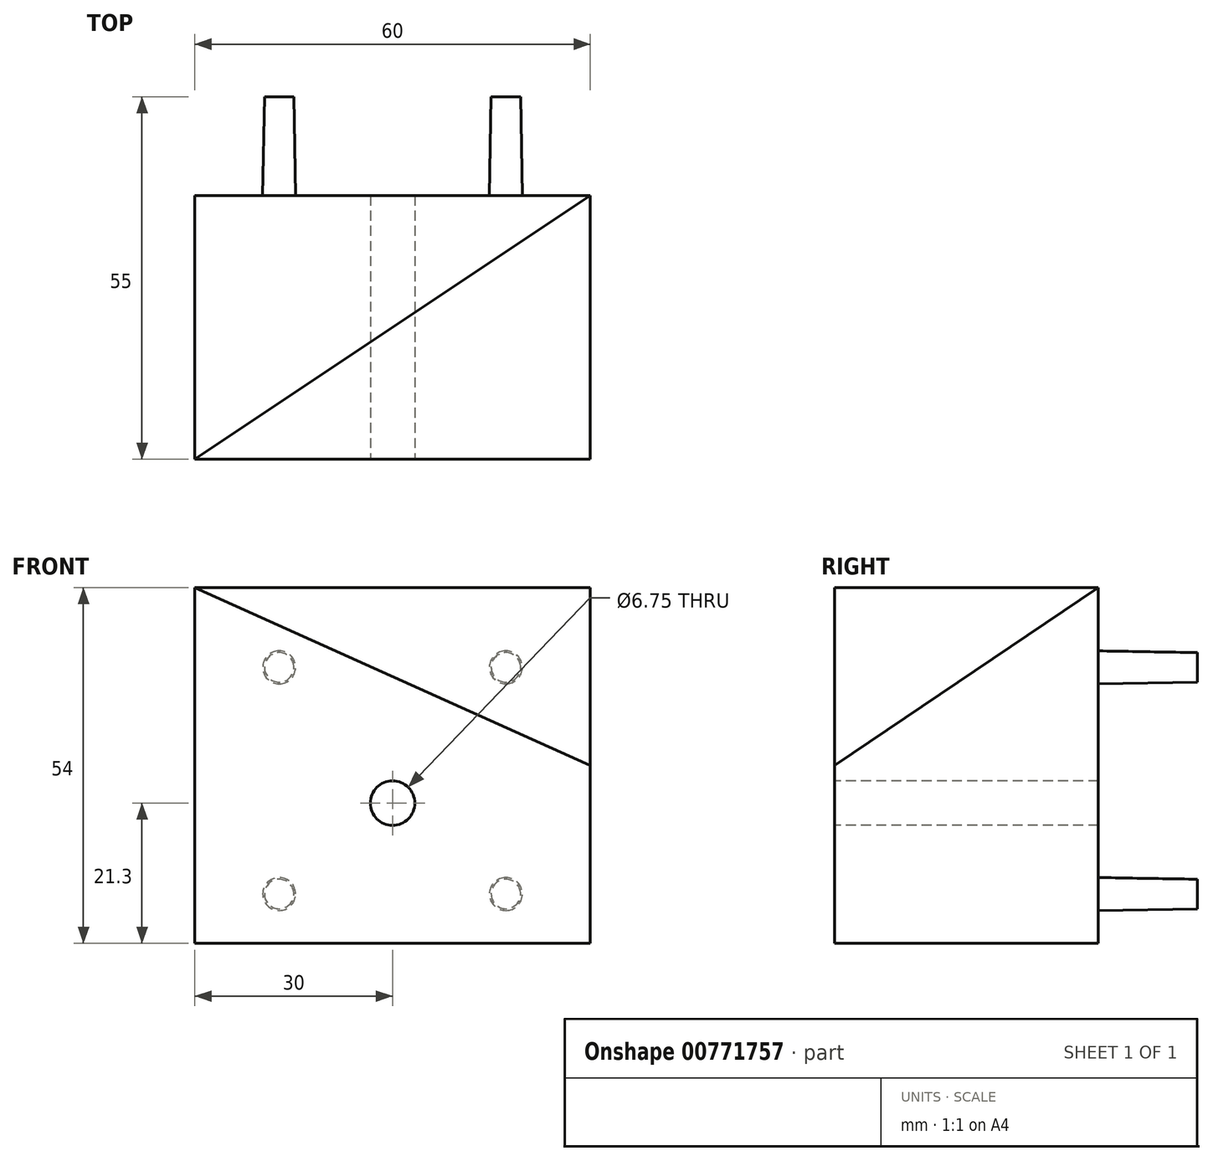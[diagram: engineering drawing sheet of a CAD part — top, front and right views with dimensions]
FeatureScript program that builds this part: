
annotation { "Feature Type Name" : "Feature", "Feature Type Description" : "" }
export const myFeature = defineFeature(function(context is Context, id is Id, definition is map)
    precondition{}
    {
        {
            var Q0;
            Q0=qCreatedBy(makeId("Front.planeOp"),FACE);
            var sketch = newSketch(context, id + "F0", { "sketchPlane" : qUnion([Q0])});
            skLineSegment(sketch, "E0.bottom", {"start": v(30, 27) * mm, "end": v(-30, 27) * mm});
            skLineSegment(sketch, "E0.top", {"start": v(30, -27) * mm, "end": v(-30, -27) * mm});
            skLineSegment(sketch, "E0.left", {"start": v(30, 27) * mm, "end": v(30, -27) * mm});
            skLineSegment(sketch, "E0.right", {"start": v(-30, 27) * mm, "end": v(-30, -27) * mm});
            skPoint(sketch, "E0.middle", {"position": v(0, 0) * mm});
            skSolve(sketch);
        }
        {
            var Q0;
            Q0=makeQuery(id+"F0.imprint","IMPRINT",FACE,{"disambiguationData":[TD([[makeQuery(id+"F0.imprint","IMPRINT",EDGE,{"derivedFrom":sQuery(id+"F0.wireOp",EDGE,"E0.bottom")}),1.0]])]});
            extrude(context, id + "F1", {"entities" : qUnion([Q0]), "depth" : 40 * mm, "offsetDistance" : 25 * mm});
        }
        {
            var Q0;
            Q0=makeQuery(id+"F1.opExtrude","CAP_FACE",FACE,{"disambiguationData":[OSD([sQuery(id+"F0.wireOp",EDGE,"E0.bottom"),sQuery(id+"F0.wireOp",EDGE,"E0.top"),sQuery(id+"F0.wireOp",EDGE,"E0.left"),sQuery(id+"F0.wireOp",EDGE,"E0.right")])],"isStart":true});
            var sketch = newSketch(context, id + "F2", { "sketchPlane" : qUnion([Q0])});
            skCircle(sketch, "E1", {"center": v(17.2, -19.5) * mm, "radius": 2.5 * mm});
            skCircle(sketch, "E2", {"center": v(-17.2, -19.5) * mm, "radius": 2.5 * mm});
            skCircle(sketch, "E3", {"center": v(-17.2, 14.9) * mm, "radius": 2.5 * mm});
            skCircle(sketch, "E4", {"center": v(17.2, 14.9) * mm, "radius": 2.5 * mm});
            skLineSegment(sketch, "E5", {"start": v(0, 0) * mm, "end": v(0, -31.74) * mm, "construction": true});
            skSolve(sketch);
        }
        {
            var Q0;
            Q0=makeQuery(id+"F2.imprint","IMPRINT",FACE,{"disambiguationData":[TD([[makeQuery(id+"F2.imprint","IMPRINT",EDGE,{"derivedFrom":sQuery(id+"F2.wireOp",EDGE,"E3")}),1.0]])]});
            var Q1;
            Q1=makeQuery(id+"F2.imprint","IMPRINT",FACE,{"disambiguationData":[TD([[makeQuery(id+"F2.imprint","IMPRINT",EDGE,{"derivedFrom":sQuery(id+"F2.wireOp",EDGE,"E4")}),1.0]])]});
            var Q2;
            Q2=makeQuery(id+"F2.imprint","IMPRINT",FACE,{"disambiguationData":[TD([[makeQuery(id+"F2.imprint","IMPRINT",EDGE,{"derivedFrom":sQuery(id+"F2.wireOp",EDGE,"E1")}),1.0]])]});
            var Q3;
            Q3=makeQuery(id+"F2.imprint","IMPRINT",FACE,{"disambiguationData":[TD([[makeQuery(id+"F2.imprint","IMPRINT",EDGE,{"derivedFrom":sQuery(id+"F2.wireOp",EDGE,"E2")}),1.0]])]});
            extrude(context, id + "F3", {"entities" : qUnion([Q0, Q1, Q2, Q3]), "operationType" : NewBodyOperationType.ADD, "depth" : 15 * mm, "offsetDistance" : 25 * mm, "hasDraft" : true, "draftAngle" : 1 * degree, "draftPullDirection" : true});
        }
        {
            var Q0;
            Q0=makeQuery(id+"F1.opExtrude","CAP_FACE",FACE,{"disambiguationData":[OSD([sQuery(id+"F0.wireOp",EDGE,"E0.bottom"),sQuery(id+"F0.wireOp",EDGE,"E0.top"),sQuery(id+"F0.wireOp",EDGE,"E0.left"),sQuery(id+"F0.wireOp",EDGE,"E0.right")])],"isStart":false});
            var sketch = newSketch(context, id + "F4", { "sketchPlane" : qUnion([Q0])});
            skCircle(sketch, "E6", {"center": v(0, -5.7) * mm, "radius": 3.38 * mm});
            skPoint(sketch, "E6.centerSnap0", {"position": v(0, -27) * mm});
            skSolve(sketch);
        }
        {
            var Q0;
            Q0=makeQuery(id+"F4.imprint","IMPRINT",FACE,{"disambiguationData":[TD([[makeQuery(id+"F4.imprint","IMPRINT",EDGE,{"derivedFrom":sQuery(id+"F4.wireOp",EDGE,"E6")}),1.0]])]});
            var Q1;
            Q1=makeQuery(id+"F1.opExtrude","CAP_FACE",FACE,{"disambiguationData":[OSD([sQuery(id+"F0.wireOp",EDGE,"E0.bottom"),sQuery(id+"F0.wireOp",EDGE,"E0.top"),sQuery(id+"F0.wireOp",EDGE,"E0.left"),sQuery(id+"F0.wireOp",EDGE,"E0.right")])],"isStart":true});
            extrude(context, id + "F5", {"entities" : qUnion([Q0]), "operationType" : NewBodyOperationType.REMOVE, "endBound" : BoundingType.UP_TO_SURFACE, "oppositeDirection" : true, "depth" : 25 * mm, "endBoundEntityFace" : qUnion([Q1]), "offsetDistance" : 25 * mm});
        }
        {
            var Q0;
            Q0=makeQuery(id+"F1.opExtrude","CAP_EDGE",EDGE,{"disambiguationData":[OSD([sQuery(id+"F0.wireOp",EDGE,"E0.left")])],"isStart":false});
            cPoint(context, id + "F6", {"entities" : qUnion([Q0]), "parameter" : 0.5});
        }
        {
            var Q0;
            Q0=makeQuery(id+"F1.opExtrude","CAP_VERTEX",VERTEX,{"disambiguationData":[OSD([sQuery(id+"F0.wireOp",EDGE,"E0.bottom"),sQuery(id+"F0.wireOp",EDGE,"E0.right")])],"isStart":false});
            var Q1;
            Q1=makeQuery(id+"F1.opExtrude","CAP_VERTEX",VERTEX,{"disambiguationData":[OSD([sQuery(id+"F0.wireOp",EDGE,"E0.bottom"),sQuery(id+"F0.wireOp",EDGE,"E0.left")])],"isStart":true});
            var Q2;
            Q2 = qCreatedBy(id + "F6" ,VERTEX);
            cPlane(context, id + "F7", {"entities" : qUnion([Q0, Q1, Q2]), "cplaneType" : CPlaneType.THREE_POINT, "offset" : 25 * mm, "width" : 150 * mm, "height" : 150 * mm});
        }
        {
            var Q0;
            Q0=qCreatedBy(id+"F7.planeOp",FACE);
            var sketch = newSketch(context, id + "F8", { "sketchPlane" : qUnion([Q0])});
            skLineSegment(sketch, "E7.bottom", {"start": v(-45.3, 19.17) * mm, "end": v(37.9, 19.17) * mm});
            skLineSegment(sketch, "E7.top", {"start": v(-45.3, -40.28) * mm, "end": v(37.9, -40.28) * mm});
            skLineSegment(sketch, "E7.left", {"start": v(-45.3, 19.17) * mm, "end": v(-45.3, -40.28) * mm});
            skLineSegment(sketch, "E7.right", {"start": v(37.9, 19.17) * mm, "end": v(37.9, -40.28) * mm});
            skSolve(sketch);
        }
        {
            var Q0;
            Q0=makeQuery(id+"F8.imprint","IMPRINT",FACE,{"disambiguationData":[TD([[makeQuery(id+"F8.imprint","IMPRINT",EDGE,{"derivedFrom":sQuery(id+"F8.wireOp",EDGE,"E7.bottom")}),-1.0]])]});
            extrude(context, id + "F9", {"entities" : qUnion([Q0]), "operationType" : NewBodyOperationType.REMOVE, "depth" : 25 * mm, "offsetDistance" : 25 * mm});
        }
    });
